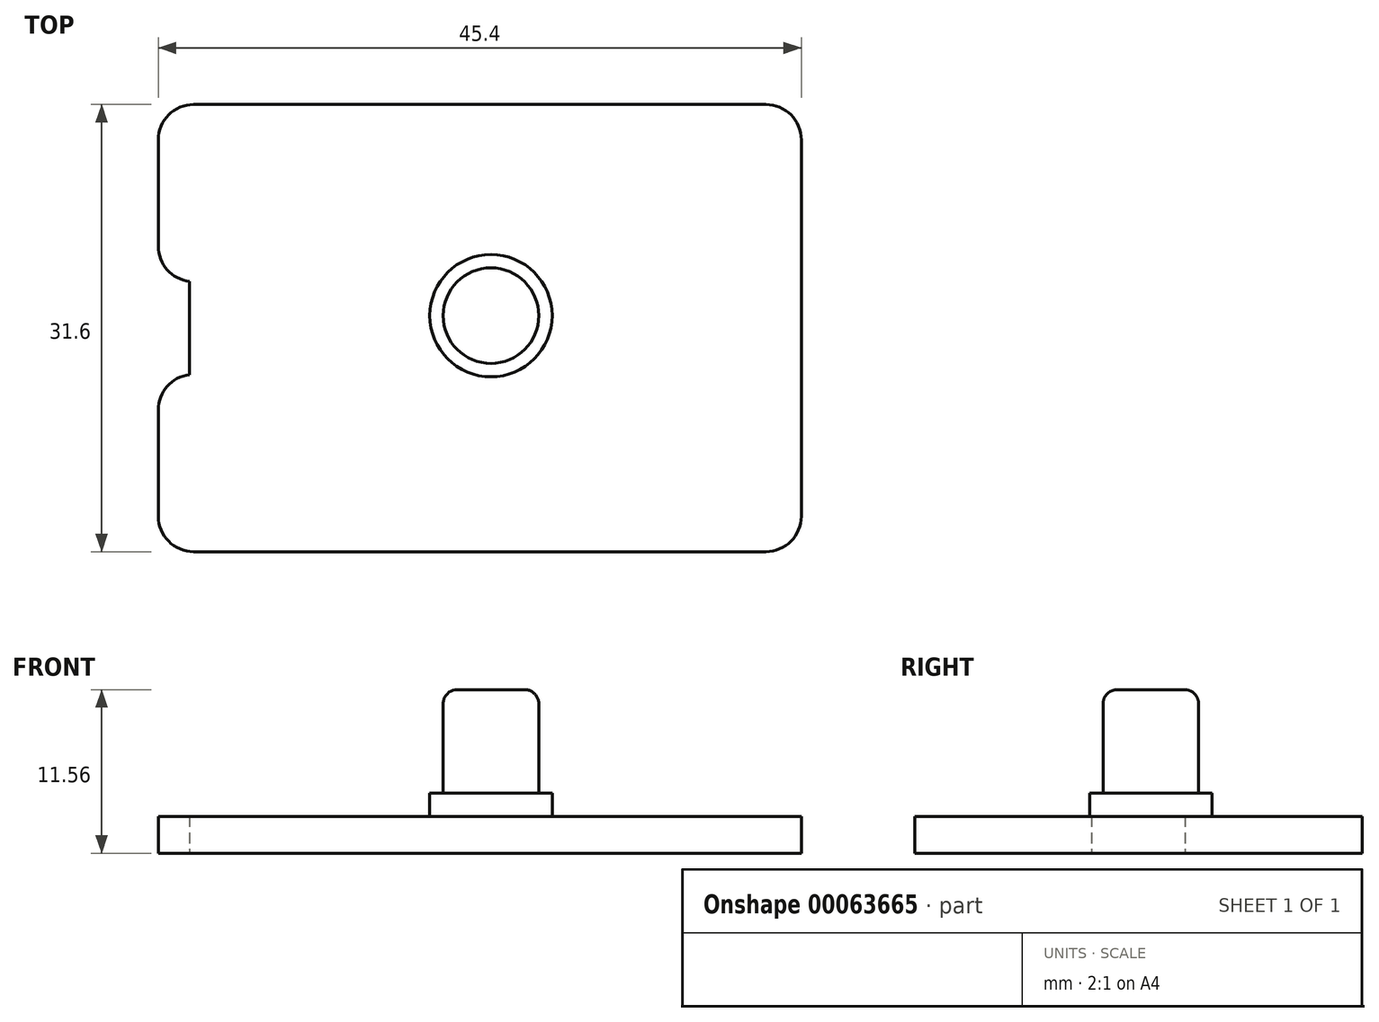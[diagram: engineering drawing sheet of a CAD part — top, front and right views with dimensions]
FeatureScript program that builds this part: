
annotation { "Feature Type Name" : "Feature", "Feature Type Description" : "" }
export const myFeature = defineFeature(function(context is Context, id is Id, definition is map)
    precondition{}
    {
        {
            var Q0;
            Q0=qCreatedBy(makeId("Top.planeOp"),FACE);
            var sketch = newSketch(context, id + "F0", { "sketchPlane" : qUnion([Q0])});
            skLineSegment(sketch, "E0.bottom", {"start": v(0, 0) * mm, "end": v(45.4, 0) * mm});
            skLineSegment(sketch, "E0.top", {"start": v(0, 31.6) * mm, "end": v(45.4, 31.6) * mm});
            skLineSegment(sketch, "E0.left", {"start": v(0, 0) * mm, "end": v(0, 12.5) * mm});
            skLineSegment(sketch, "E0.right", {"start": v(45.4, 0) * mm, "end": v(45.4, 31.6) * mm});
            skLineSegment(sketch, "E1.bottom", {"start": v(0, 19.1) * mm, "end": v(2.2, 19.1) * mm});
            skLineSegment(sketch, "E1.top", {"start": v(0, 12.5) * mm, "end": v(2.2, 12.5) * mm});
            skLineSegment(sketch, "E1.right", {"start": v(2.2, 19.1) * mm, "end": v(2.2, 12.5) * mm});
            skLineSegment(sketch, "E2.trimOffspring", {"start": v(0, 19.1) * mm, "end": v(0, 31.6) * mm});
            skSolve(sketch);
        }
        {
            var Q0;
            Q0 = qSketchRegion(id + "F0", true);
            extrude(context, id + "F1", {"entities" : qUnion([Q0]), "depth" : 2.6 * mm});
        }
        {
            var Q0;
            Q0=makeQuery(id+"F1.opExtrude","SWEPT_EDGE",EDGE,{"disambiguationData":[OSD([sQuery(id+"F0.wireOp",EDGE,"E0.top"),sQuery(id+"F0.wireOp",EDGE,"E0.right")])]});
            var Q1;
            Q1=makeQuery(id+"F1.opExtrude","SWEPT_EDGE",EDGE,{"disambiguationData":[OSD([sQuery(id+"F0.wireOp",EDGE,"E0.top"),sQuery(id+"F0.wireOp",EDGE,"E2.trimOffspring")])]});
            var Q2;
            Q2=makeQuery(id+"F1.opExtrude","SWEPT_EDGE",EDGE,{"disambiguationData":[OSD([sQuery(id+"F0.wireOp",EDGE,"E0.bottom"),sQuery(id+"F0.wireOp",EDGE,"E0.right")])]});
            var Q3;
            Q3=makeQuery(id+"F1.opExtrude","SWEPT_EDGE",EDGE,{"disambiguationData":[OSD([sQuery(id+"F0.wireOp",EDGE,"E0.bottom"),sQuery(id+"F0.wireOp",EDGE,"E0.left")])]});
            var Q4;
            Q4=makeQuery(id+"F1.opExtrude","SWEPT_EDGE",EDGE,{"disambiguationData":[OSD([sQuery(id+"F0.wireOp",EDGE,"E1.bottom"),sQuery(id+"F0.wireOp",EDGE,"E2.trimOffspring")])]});
            var Q5;
            Q5=makeQuery(id+"F1.opExtrude","SWEPT_EDGE",EDGE,{"disambiguationData":[OSD([sQuery(id+"F0.wireOp",EDGE,"E0.left"),sQuery(id+"F0.wireOp",EDGE,"E1.top")])]});
            fillet(context, id + "F2", {"entities" : qUnion([Q0, Q1, Q2, Q3, Q4, Q5]), "radius" : 2.5 * mm, "tangentPropagation" : true, "allowEdgeOverflow" : false});
        }
        {
            var Q0;
            Q0=makeQuery(id+"F1.opExtrude","CAP_FACE",FACE,{"disambiguationData":[OSD([sQuery(id+"F0.wireOp",EDGE,"E0.bottom"),sQuery(id+"F0.wireOp",EDGE,"E0.top"),sQuery(id+"F0.wireOp",EDGE,"E0.left"),sQuery(id+"F0.wireOp",EDGE,"E0.right"),sQuery(id+"F0.wireOp",EDGE,"E1.bottom"),sQuery(id+"F0.wireOp",EDGE,"E1.top"),sQuery(id+"F0.wireOp",EDGE,"E1.right"),sQuery(id+"F0.wireOp",EDGE,"E2.trimOffspring")])],"isStart":false});
            var sketch = newSketch(context, id + "F3", { "sketchPlane" : qUnion([Q0])});
            skCircle(sketch, "E3", {"center": v(23.49, 16.68) * mm, "radius": 4.32 * mm});
            skSolve(sketch);
        }
        {
            var Q0;
            Q0 = qSketchRegion(id + "F3", true);
            extrude(context, id + "F4", {"entities" : qUnion([Q0]), "operationType" : NewBodyOperationType.ADD, "depth" : 1.66 * mm});
        }
        {
            var Q0;
            Q0=makeQuery(id+"F4.opExtrude","CAP_FACE",FACE,{"disambiguationData":[OSD([sQuery(id+"F3.wireOp",EDGE,"E3")])],"isStart":false});
            var sketch = newSketch(context, id + "F5", { "sketchPlane" : qUnion([Q0])});
            skCircle(sketch, "E4", {"center": v(23.49, 16.68) * mm, "radius": 3.38 * mm});
            skSolve(sketch);
        }
        {
            var Q0;
            Q0 = qSketchRegion(id + "F5", true);
            extrude(context, id + "F6", {"entities" : qUnion([Q0]), "operationType" : NewBodyOperationType.ADD, "depth" : (11.6 - 4.3) * mm});
        }
        {
            var Q0;
            Q0=makeQuery(id+"F6.opExtrude","CAP_EDGE",EDGE,{"disambiguationData":[OSD([sQuery(id+"F5.wireOp",EDGE,"E4")])],"isStart":false});
            fillet(context, id + "F7", {"entities" : qUnion([Q0]), "radius" : 1 * mm, "tangentPropagation" : true, "allowEdgeOverflow" : false});
        }
    });
